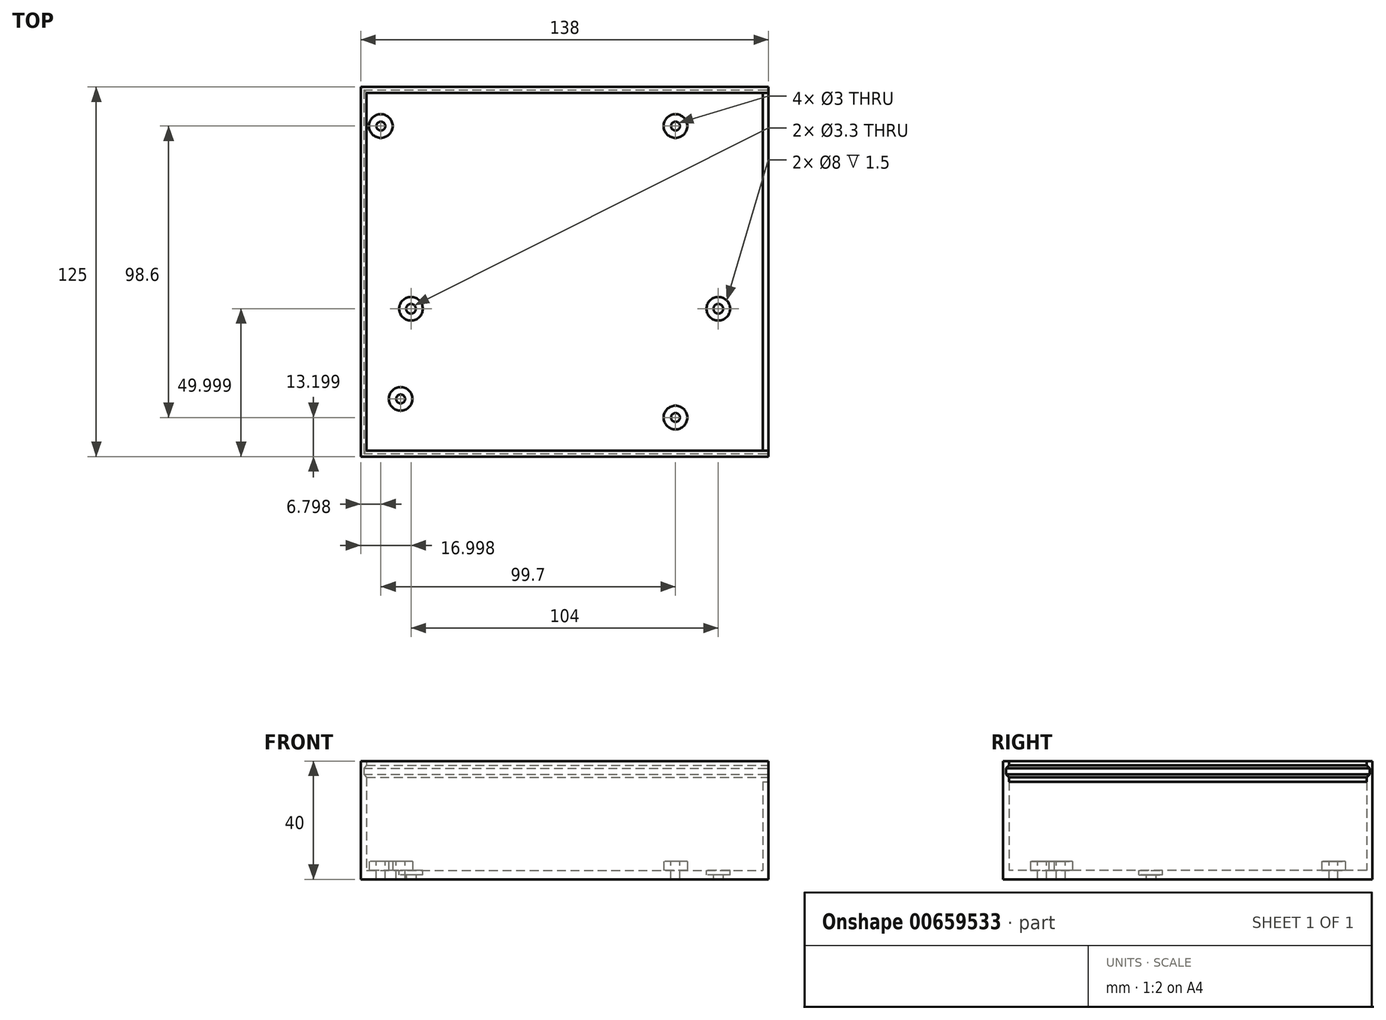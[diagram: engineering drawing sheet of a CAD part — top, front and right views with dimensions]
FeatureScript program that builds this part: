
annotation { "Feature Type Name" : "Feature", "Feature Type Description" : "" }
export const myFeature = defineFeature(function(context is Context, id is Id, definition is map)
    precondition{}
    {
        {
            var Q0;
            Q0=qCreatedBy(makeId("Top.planeOp"),FACE);
            var sketch = newSketch(context, id + "F0", { "sketchPlane" : qUnion([Q0])});
            skLineSegment(sketch, "E0.bottom", {"start": v(-34.98, -21.82) * mm, "end": v(103.02, -21.82) * mm});
            skLineSegment(sketch, "E0.top", {"start": v(-34.98, -146.82) * mm, "end": v(103.02, -146.82) * mm});
            skLineSegment(sketch, "E0.left", {"start": v(-34.98, -21.82) * mm, "end": v(-34.98, -146.82) * mm});
            skLineSegment(sketch, "E0.right", {"start": v(103.02, -21.82) * mm, "end": v(103.02, -146.82) * mm});
            skCircle(sketch, "E1", {"center": v(-17.98, -96.82) * mm, "radius": 1.65 * mm});
            skCircle(sketch, "E2", {"center": v(86.02, -96.82) * mm, "radius": 1.65 * mm});
            skSolve(sketch);
        }
        {
            var Q0;
            Q0 = qSketchRegion(id + "F0", true);
            extrude(context, id + "F1", {"entities" : qUnion([Q0]), "depth" : 3 * mm, "offsetDistance" : 25 * mm});
        }
        {
            var Q0;
            Q0=makeQuery(id+"F1.opExtrude","CAP_FACE",FACE,{"disambiguationData":[OSD([sQuery(id+"F0.wireOp",EDGE,"E0.bottom"),sQuery(id+"F0.wireOp",EDGE,"E0.top"),sQuery(id+"F0.wireOp",EDGE,"E0.left"),sQuery(id+"F0.wireOp",EDGE,"E0.right"),sQuery(id+"F0.wireOp",EDGE,"E1"),sQuery(id+"F0.wireOp",EDGE,"E2")])],"isStart":false});
            var sketch = newSketch(context, id + "F2", { "sketchPlane" : qUnion([Q0])});
            skCircle(sketch, "E3", {"center": v(-17.98, -96.82) * mm, "radius": 4 * mm});
            skCircle(sketch, "E4", {"center": v(86.02, -96.82) * mm, "radius": 4 * mm});
            skSolve(sketch);
        }
        {
            var Q0;
            Q0 = qSketchRegion(id + "F2", true);
            extrude(context, id + "F3", {"entities" : qUnion([Q0]), "operationType" : NewBodyOperationType.REMOVE, "oppositeDirection" : true, "depth" : 1.5 * mm, "offsetDistance" : 25 * mm});
        }
        {
            var Q0;
            Q0=makeQuery(id+"F1.opExtrude","CAP_FACE",FACE,{"disambiguationData":[OSD([sQuery(id+"F0.wireOp",EDGE,"E0.bottom"),sQuery(id+"F0.wireOp",EDGE,"E0.top"),sQuery(id+"F0.wireOp",EDGE,"E0.left"),sQuery(id+"F0.wireOp",EDGE,"E0.right"),sQuery(id+"F0.wireOp",EDGE,"E1"),sQuery(id+"F0.wireOp",EDGE,"E2")])],"isStart":false});
            var sketch = newSketch(context, id + "F4", { "sketchPlane" : qUnion([Q0])});
            skCircle(sketch, "E5", {"center": v(-21.48, -127.32) * mm, "radius": 4 * mm});
            skCircle(sketch, "E6", {"center": v(-28.18, -35.02) * mm, "radius": 4 * mm});
            skCircle(sketch, "E7", {"center": v(71.52, -35.02) * mm, "radius": 4 * mm});
            skCircle(sketch, "E8", {"center": v(71.52, -133.62) * mm, "radius": 4 * mm});
            skLineSegment(sketch, "E9.bottom", {"start": v(-30.98, -31.82) * mm, "end": v(99.02, -31.82) * mm, "construction": true});
            skLineSegment(sketch, "E9.top", {"start": v(-30.98, -136.82) * mm, "end": v(99.02, -136.82) * mm, "construction": true});
            skLineSegment(sketch, "E9.left", {"start": v(-30.98, -31.82) * mm, "end": v(-30.98, -136.82) * mm, "construction": true});
            skLineSegment(sketch, "E9.right", {"start": v(99.02, -31.82) * mm, "end": v(99.02, -136.82) * mm, "construction": true});
            skSolve(sketch);
        }
        {
            var Q0;
            Q0 = qSketchRegion(id + "F4", true);
            extrude(context, id + "F5", {"entities" : qUnion([Q0]), "operationType" : NewBodyOperationType.ADD, "depth" : 3 * mm, "offsetDistance" : 25 * mm});
        }
        {
            var Q0;
            Q0=makeQuery(id+"F5.opExtrude","CAP_FACE",FACE,{"disambiguationData":[OSD([sQuery(id+"F4.wireOp",EDGE,"E6")])],"isStart":false});
            var sketch = newSketch(context, id + "F6", { "sketchPlane" : qUnion([Q0])});
            skCircle(sketch, "E10", {"center": v(-28.18, -35.02) * mm, "radius": 1.5 * mm});
            skCircle(sketch, "E11", {"center": v(71.52, -35.02) * mm, "radius": 1.5 * mm});
            skCircle(sketch, "E12", {"center": v(71.52, -133.62) * mm, "radius": 1.5 * mm});
            skCircle(sketch, "E13", {"center": v(-21.48, -127.32) * mm, "radius": 1.5 * mm});
            skSolve(sketch);
        }
        {
            var Q0;
            Q0 = qSketchRegion(id + "F6", true);
            extrude(context, id + "F7", {"entities" : qUnion([Q0]), "operationType" : NewBodyOperationType.REMOVE, "oppositeDirection" : true, "depth" : 6 * mm, "offsetDistance" : 25 * mm});
        }
        {
            var Q0;
            Q0=makeQuery(id+"F4.imprint","IMPRINT",FACE,{"disambiguationData":[TD([[makeQuery(id+"F4.imprint","IMPRINT",EDGE,{"derivedFrom":sQuery(id+"F4.wireOp",EDGE,"E5")}),-1.0]])]});
            var sketch = newSketch(context, id + "F8", { "sketchPlane" : qUnion([Q0])});
            skLineSegment(sketch, "E14.bottom", {"start": v(103.02, -21.82) * mm, "end": v(-34.98, -21.82) * mm});
            skLineSegment(sketch, "E14.top", {"start": v(103.02, -146.82) * mm, "end": v(-34.98, -146.82) * mm});
            skLineSegment(sketch, "E14.left", {"start": v(103.02, -21.82) * mm, "end": v(103.02, -146.82) * mm});
            skLineSegment(sketch, "E14.right", {"start": v(-34.98, -21.82) * mm, "end": v(-34.98, -146.82) * mm});
            skLineSegment(sketch, "E15.bottom", {"start": v(-32.98, -23.82) * mm, "end": v(101.02, -23.82) * mm});
            skLineSegment(sketch, "E15.top", {"start": v(-32.98, -144.82) * mm, "end": v(101.02, -144.82) * mm});
            skLineSegment(sketch, "E15.left", {"start": v(-32.98, -23.82) * mm, "end": v(-32.98, -144.82) * mm});
            skLineSegment(sketch, "E15.right", {"start": v(101.02, -23.82) * mm, "end": v(101.02, -144.82) * mm});
            skSolve(sketch);
        }
        {
            var Q0;
            Q0 = qSketchRegion(id + "F8", true);
            extrude(context, id + "F9", {"entities" : qUnion([Q0]), "operationType" : NewBodyOperationType.ADD, "depth" : 30 * mm, "offsetDistance" : 25 * mm});
        }
        {
            var Q0;
            Q0=makeQuery(id+"F9.boolean.opBoolean","MERGE",FACE,{"derivedFrom":[makeQuery(id+"F1.opExtrude","SWEPT_FACE",FACE,{"disambiguationData":[OSD([sQuery(id+"F0.wireOp",EDGE,"E0.right")])]}),makeQuery(id+"F9.opExtrude","SWEPT_FACE",FACE,{"disambiguationData":[OSD([sQuery(id+"F8.wireOp",EDGE,"E14.left")])]})]});
            var sketch = newSketch(context, id + "F10", { "sketchPlane" : qUnion([Q0])});
            skLineSegment(sketch, "E16", {"start": v(-146.82, 33) * mm, "end": v(-146.82, 40) * mm});
            skLineSegment(sketch, "E17", {"start": v(-146.82, 40) * mm, "end": v(-144.82, 40) * mm});
            skLineSegment(sketch, "E18", {"start": v(-144.82, 40) * mm, "end": v(-144.82, 38.5) * mm});
            skLineSegment(sketch, "E19", {"start": v(-144.82, 38.5) * mm, "end": v(-145.82, 37.5) * mm});
            skLineSegment(sketch, "E20", {"start": v(-145.82, 37.5) * mm, "end": v(-145.82, 35.5) * mm});
            skLineSegment(sketch, "E21", {"start": v(-145.82, 35.5) * mm, "end": v(-144.82, 34.5) * mm});
            skLineSegment(sketch, "E22", {"start": v(-144.82, 34.5) * mm, "end": v(-144.82, 33) * mm});
            skLineSegment(sketch, "E23", {"start": v(-144.82, 33) * mm, "end": v(-146.82, 33) * mm});
            skLineSegment(sketch, "E24", {"start": v(-84.32, 33) * mm, "end": v(-84.32, 0) * mm, "construction": true});
            skLineSegment(sketch, "E25.MirrorCS", {"start": v(-23.82, 38.5) * mm, "end": v(-22.82, 37.5) * mm});
            skLineSegment(sketch, "E26.MirrorCS", {"start": v(-23.82, 33) * mm, "end": v(-21.82, 33) * mm});
            skLineSegment(sketch, "E27.MirrorCS", {"start": v(-23.82, 34.5) * mm, "end": v(-23.82, 33) * mm});
            skLineSegment(sketch, "E28.MirrorCS", {"start": v(-22.82, 35.5) * mm, "end": v(-23.82, 34.5) * mm});
            skLineSegment(sketch, "E29.MirrorCS", {"start": v(-23.82, 40) * mm, "end": v(-23.82, 38.5) * mm});
            skLineSegment(sketch, "E30.MirrorCS", {"start": v(-22.82, 37.5) * mm, "end": v(-22.82, 35.5) * mm});
            skLineSegment(sketch, "E31.MirrorCS", {"start": v(-21.82, 33) * mm, "end": v(-21.82, 40) * mm});
            skLineSegment(sketch, "E32.MirrorCS", {"start": v(-21.82, 40) * mm, "end": v(-23.82, 40) * mm});
            skSolve(sketch);
        }
        {
            var Q0;
            Q0 = qSketchRegion(id + "F10", true);
            extrude(context, id + "F11", {"entities" : qUnion([Q0]), "operationType" : NewBodyOperationType.ADD, "oppositeDirection" : true, "depth" : 138 * mm, "offsetDistance" : 25 * mm});
        }
        {
            var Q0;
            Q0=makeQuery(id+"F11.boolean.opBoolean","MERGE",FACE,{"derivedFrom":[makeQuery(id+"F9.boolean.opBoolean","MERGE",FACE,{"derivedFrom":[makeQuery(id+"F1.opExtrude","SWEPT_FACE",FACE,{"disambiguationData":[OSD([sQuery(id+"F0.wireOp",EDGE,"E0.top")])]}),makeQuery(id+"F9.opExtrude","SWEPT_FACE",FACE,{"disambiguationData":[OSD([sQuery(id+"F8.wireOp",EDGE,"E14.top")])]})]}),makeQuery(id+"F11.opExtrude","SWEPT_FACE",FACE,{"disambiguationData":[OSD([sQuery(id+"F10.wireOp",EDGE,"E16")])]})]});
            var sketch = newSketch(context, id + "F12", { "sketchPlane" : qUnion([Q0])});
            skLineSegment(sketch, "E33", {"start": v(-34.98, 33) * mm, "end": v(-34.98, 40) * mm});
            skLineSegment(sketch, "E34", {"start": v(-34.98, 40) * mm, "end": v(-32.98, 40) * mm});
            skLineSegment(sketch, "E35", {"start": v(-32.98, 40) * mm, "end": v(-32.98, 38.5) * mm});
            skLineSegment(sketch, "E36", {"start": v(-32.98, 38.5) * mm, "end": v(-33.98, 37.5) * mm});
            skLineSegment(sketch, "E37", {"start": v(-33.98, 37.5) * mm, "end": v(-33.98, 35.5) * mm});
            skLineSegment(sketch, "E38", {"start": v(-33.98, 35.5) * mm, "end": v(-32.98, 34.5) * mm});
            skLineSegment(sketch, "E39", {"start": v(-32.98, 34.5) * mm, "end": v(-32.98, 33) * mm});
            skLineSegment(sketch, "E40", {"start": v(-32.98, 33) * mm, "end": v(-34.98, 33) * mm});
            skSolve(sketch);
        }
        {
            var Q0;
            Q0 = qSketchRegion(id + "F12", true);
            extrude(context, id + "F13", {"entities" : qUnion([Q0]), "operationType" : NewBodyOperationType.ADD, "oppositeDirection" : true, "depth" : 125 * mm, "offsetDistance" : 25 * mm});
        }
    });
